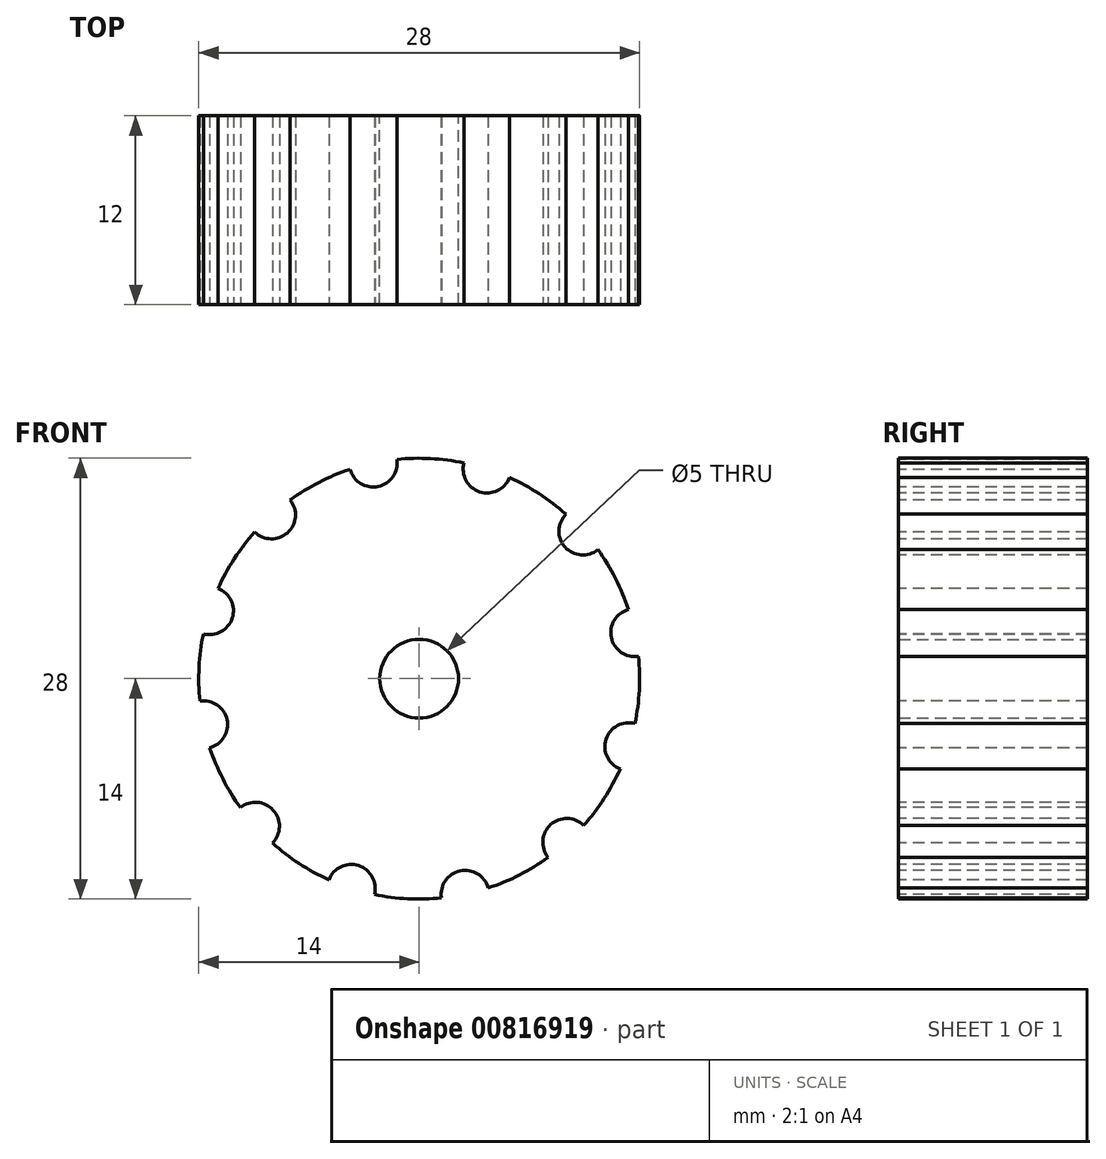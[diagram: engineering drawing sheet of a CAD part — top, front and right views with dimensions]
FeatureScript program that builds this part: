
annotation { "Feature Type Name" : "Feature", "Feature Type Description" : "" }
export const myFeature = defineFeature(function(context is Context, id is Id, definition is map)
    precondition{}
    {
        {
            var Q0;
            Q0=qCreatedBy(makeId("Front.planeOp"),FACE);
            var sketch = newSketch(context, id + "F0", { "sketchPlane" : qUnion([Q0])});
            skPoint(sketch, "E0", {"position": v(0, 0) * mm});
            skCircle(sketch, "E1", {"center": v(0, 0) * mm, "radius": 14 * mm});
            skCircle(sketch, "E2", {"center": v(-7.82, 11.61) * mm, "radius": 1.64 * mm});
            skSolve(sketch);
        }
        {
            var Q0;
            {var subQ0=sQuery(id+"F0.wireOp",EDGE,"E2");var subQ1=sQuery(id+"F0.wireOp",EDGE,"E1");var subQ2=makeQuery(id+"F0.imprint","INTERSECT",VERTEX,{"disambiguationData":[OD(0.0)],"derivedFrom":[subQ1,subQ0]});Q0=makeQuery(id+"F0.imprint","IMPRINT",FACE,{"disambiguationData":[TD([[makeQuery(id+"F0.imprint","IMPRINT",EDGE,{"disambiguationData":[TD([[subQ2,-1.0]])],"derivedFrom":subQ1}),1.0]])]});}
            var Q1;
            {var subQ0=sQuery(id+"F0.wireOp",EDGE,"E2");var subQ1=sQuery(id+"F0.wireOp",EDGE,"E1");var subQ2=makeQuery(id+"F0.imprint","INTERSECT",VERTEX,{"disambiguationData":[OD(0.0)],"derivedFrom":[subQ1,subQ0]});Q1=makeQuery(id+"F0.imprint","IMPRINT",FACE,{"disambiguationData":[TD([[makeQuery(id+"F0.imprint","IMPRINT",EDGE,{"disambiguationData":[TD([[subQ2,1.0]])],"derivedFrom":subQ1}),1.0]])]});}
            extrude(context, id + "F1", {"entities" : qUnion([Q0, Q1]), "depth" : 12 * mm, "offsetDistance" : 25 * mm});
        }
        {
            var Q0;
            Q0=makeQuery(id+"F1.opExtrude","CAP_FACE",FACE,{"disambiguationData":[OSD([sQuery(id+"F0.wireOp",EDGE,"E1")])],"isStart":false});
            var sketch = newSketch(context, id + "F2", { "sketchPlane" : qUnion([Q0])});
            skCircle(sketch, "E3", {"center": v(-9.38, 10.4) * mm, "radius": 1.52 * mm});
            skCircle(sketch, "E4.1.0", {"center": v(-13.32, 4.32) * mm, "radius": 1.52 * mm});
            skCircle(sketch, "E4.2.0", {"center": v(-13.7, -2.92) * mm, "radius": 1.52 * mm});
            skCircle(sketch, "E4.3.0", {"center": v(-10.4, -9.38) * mm, "radius": 1.52 * mm});
            skCircle(sketch, "E4.4.0", {"center": v(-4.32, -13.32) * mm, "radius": 1.52 * mm});
            skCircle(sketch, "E4.5.0", {"center": v(2.92, -13.7) * mm, "radius": 1.52 * mm});
            skCircle(sketch, "E4.6.0", {"center": v(9.38, -10.4) * mm, "radius": 1.52 * mm});
            skCircle(sketch, "E4.7.0", {"center": v(13.32, -4.32) * mm, "radius": 1.52 * mm});
            skCircle(sketch, "E4.8.0", {"center": v(13.7, 2.92) * mm, "radius": 1.52 * mm});
            skCircle(sketch, "E4.9.0", {"center": v(10.4, 9.38) * mm, "radius": 1.52 * mm});
            skCircle(sketch, "E4.10.0", {"center": v(4.32, 13.32) * mm, "radius": 1.52 * mm});
            skCircle(sketch, "E4.11.0", {"center": v(-2.92, 13.7) * mm, "radius": 1.52 * mm});
            skPoint(sketch, "E4.center", {"position": v(0, 0) * mm});
            skSolve(sketch);
        }
        {
            var Q0;
            {var subQ0=sQuery(id+"F2.wireOp",EDGE,"E4.10.0");var subQ1=makeQuery(id+"F1.opExtrude","CAP_EDGE",EDGE,{"disambiguationData":[OSD([sQuery(id+"F0.wireOp",EDGE,"E1")])],"isStart":false});var subQ2=makeQuery(id+"F2.imprint","INTERSECT",VERTEX,{"disambiguationData":[OD(0.0)],"derivedFrom":[subQ1,subQ0]});Q0=makeQuery(id+"F2.imprint","IMPRINT",FACE,{"disambiguationData":[TD([[makeQuery(id+"F2.imprint","IMPRINT",EDGE,{"disambiguationData":[TD([[subQ2,1.0]])],"derivedFrom":subQ0}),1.0]])]});}
            var Q1;
            {var subQ0=sQuery(id+"F2.wireOp",EDGE,"E4.10.0");var subQ1=makeQuery(id+"F1.opExtrude","CAP_EDGE",EDGE,{"disambiguationData":[OSD([sQuery(id+"F0.wireOp",EDGE,"E1")])],"isStart":false});var subQ2=makeQuery(id+"F2.imprint","INTERSECT",VERTEX,{"disambiguationData":[OD(0.0)],"derivedFrom":[subQ1,subQ0]});Q1=makeQuery(id+"F2.imprint","IMPRINT",FACE,{"disambiguationData":[TD([[makeQuery(id+"F2.imprint","IMPRINT",EDGE,{"disambiguationData":[TD([[subQ2,-1.0]])],"derivedFrom":subQ0}),1.0]])]});}
            var Q2;
            {var subQ0=sQuery(id+"F2.wireOp",EDGE,"E4.9.0");var subQ1=makeQuery(id+"F1.opExtrude","CAP_EDGE",EDGE,{"disambiguationData":[OSD([sQuery(id+"F0.wireOp",EDGE,"E1")])],"isStart":false});var subQ2=makeQuery(id+"F2.imprint","INTERSECT",VERTEX,{"disambiguationData":[OD(0.0)],"derivedFrom":[subQ1,subQ0]});Q2=makeQuery(id+"F2.imprint","IMPRINT",FACE,{"disambiguationData":[TD([[makeQuery(id+"F2.imprint","IMPRINT",EDGE,{"disambiguationData":[TD([[subQ2,-1.0]])],"derivedFrom":subQ0}),1.0]])]});}
            var Q3;
            {var subQ0=sQuery(id+"F2.wireOp",EDGE,"E4.9.0");var subQ1=makeQuery(id+"F1.opExtrude","CAP_EDGE",EDGE,{"disambiguationData":[OSD([sQuery(id+"F0.wireOp",EDGE,"E1")])],"isStart":false});var subQ2=makeQuery(id+"F2.imprint","INTERSECT",VERTEX,{"disambiguationData":[OD(0.0)],"derivedFrom":[subQ1,subQ0]});Q3=makeQuery(id+"F2.imprint","IMPRINT",FACE,{"disambiguationData":[TD([[makeQuery(id+"F2.imprint","IMPRINT",EDGE,{"disambiguationData":[TD([[subQ2,1.0]])],"derivedFrom":subQ0}),1.0]])]});}
            var Q4;
            {var subQ0=sQuery(id+"F2.wireOp",EDGE,"E4.8.0");var subQ1=makeQuery(id+"F1.opExtrude","CAP_EDGE",EDGE,{"disambiguationData":[OSD([sQuery(id+"F0.wireOp",EDGE,"E1")])],"isStart":false});var subQ2=makeQuery(id+"F2.imprint","INTERSECT",VERTEX,{"disambiguationData":[OD(0.0)],"derivedFrom":[subQ1,subQ0]});Q4=makeQuery(id+"F2.imprint","IMPRINT",FACE,{"disambiguationData":[TD([[makeQuery(id+"F2.imprint","IMPRINT",EDGE,{"disambiguationData":[TD([[subQ2,-1.0]])],"derivedFrom":subQ0}),1.0]])]});}
            var Q5;
            {var subQ0=sQuery(id+"F2.wireOp",EDGE,"E4.8.0");var subQ1=makeQuery(id+"F1.opExtrude","CAP_EDGE",EDGE,{"disambiguationData":[OSD([sQuery(id+"F0.wireOp",EDGE,"E1")])],"isStart":false});var subQ2=makeQuery(id+"F2.imprint","INTERSECT",VERTEX,{"disambiguationData":[OD(0.0)],"derivedFrom":[subQ1,subQ0]});Q5=makeQuery(id+"F2.imprint","IMPRINT",FACE,{"disambiguationData":[TD([[makeQuery(id+"F2.imprint","IMPRINT",EDGE,{"disambiguationData":[TD([[subQ2,1.0]])],"derivedFrom":subQ0}),1.0]])]});}
            var Q6;
            {var subQ0=sQuery(id+"F2.wireOp",EDGE,"E4.7.0");var subQ1=makeQuery(id+"F1.opExtrude","CAP_EDGE",EDGE,{"disambiguationData":[OSD([sQuery(id+"F0.wireOp",EDGE,"E1")])],"isStart":false});var subQ2=makeQuery(id+"F2.imprint","INTERSECT",VERTEX,{"disambiguationData":[OD(0.0)],"derivedFrom":[subQ1,subQ0]});Q6=makeQuery(id+"F2.imprint","IMPRINT",FACE,{"disambiguationData":[TD([[makeQuery(id+"F2.imprint","IMPRINT",EDGE,{"disambiguationData":[TD([[subQ2,1.0]])],"derivedFrom":subQ0}),1.0]])]});}
            var Q7;
            {var subQ0=sQuery(id+"F2.wireOp",EDGE,"E4.7.0");var subQ1=makeQuery(id+"F1.opExtrude","CAP_EDGE",EDGE,{"disambiguationData":[OSD([sQuery(id+"F0.wireOp",EDGE,"E1")])],"isStart":false});var subQ2=makeQuery(id+"F2.imprint","INTERSECT",VERTEX,{"disambiguationData":[OD(0.0)],"derivedFrom":[subQ1,subQ0]});Q7=makeQuery(id+"F2.imprint","IMPRINT",FACE,{"disambiguationData":[TD([[makeQuery(id+"F2.imprint","IMPRINT",EDGE,{"disambiguationData":[TD([[subQ2,-1.0]])],"derivedFrom":subQ0}),1.0]])]});}
            var Q8;
            {var subQ0=sQuery(id+"F2.wireOp",EDGE,"E4.6.0");var subQ1=makeQuery(id+"F1.opExtrude","CAP_EDGE",EDGE,{"disambiguationData":[OSD([sQuery(id+"F0.wireOp",EDGE,"E1")])],"isStart":false});var subQ2=makeQuery(id+"F2.imprint","INTERSECT",VERTEX,{"disambiguationData":[OD(0.0)],"derivedFrom":[subQ1,subQ0]});Q8=makeQuery(id+"F2.imprint","IMPRINT",FACE,{"disambiguationData":[TD([[makeQuery(id+"F2.imprint","IMPRINT",EDGE,{"disambiguationData":[TD([[subQ2,1.0]])],"derivedFrom":subQ0}),1.0]])]});}
            var Q9;
            {var subQ0=sQuery(id+"F2.wireOp",EDGE,"E4.5.0");var subQ1=makeQuery(id+"F1.opExtrude","CAP_EDGE",EDGE,{"disambiguationData":[OSD([sQuery(id+"F0.wireOp",EDGE,"E1")])],"isStart":false});var subQ2=makeQuery(id+"F2.imprint","INTERSECT",VERTEX,{"disambiguationData":[OD(0.0)],"derivedFrom":[subQ1,subQ0]});Q9=makeQuery(id+"F2.imprint","IMPRINT",FACE,{"disambiguationData":[TD([[makeQuery(id+"F2.imprint","IMPRINT",EDGE,{"disambiguationData":[TD([[subQ2,-1.0]])],"derivedFrom":subQ0}),1.0]])]});}
            var Q10;
            {var subQ0=sQuery(id+"F2.wireOp",EDGE,"E4.5.0");var subQ1=makeQuery(id+"F1.opExtrude","CAP_EDGE",EDGE,{"disambiguationData":[OSD([sQuery(id+"F0.wireOp",EDGE,"E1")])],"isStart":false});var subQ2=makeQuery(id+"F2.imprint","INTERSECT",VERTEX,{"disambiguationData":[OD(0.0)],"derivedFrom":[subQ1,subQ0]});Q10=makeQuery(id+"F2.imprint","IMPRINT",FACE,{"disambiguationData":[TD([[makeQuery(id+"F2.imprint","IMPRINT",EDGE,{"disambiguationData":[TD([[subQ2,1.0]])],"derivedFrom":subQ0}),1.0]])]});}
            var Q11;
            {var subQ0=sQuery(id+"F2.wireOp",EDGE,"E4.4.0");var subQ1=makeQuery(id+"F1.opExtrude","CAP_EDGE",EDGE,{"disambiguationData":[OSD([sQuery(id+"F0.wireOp",EDGE,"E1")])],"isStart":false});var subQ2=makeQuery(id+"F2.imprint","INTERSECT",VERTEX,{"disambiguationData":[OD(0.0)],"derivedFrom":[subQ1,subQ0]});Q11=makeQuery(id+"F2.imprint","IMPRINT",FACE,{"disambiguationData":[TD([[makeQuery(id+"F2.imprint","IMPRINT",EDGE,{"disambiguationData":[TD([[subQ2,1.0]])],"derivedFrom":subQ0}),1.0]])]});}
            var Q12;
            {var subQ0=sQuery(id+"F2.wireOp",EDGE,"E4.3.0");var subQ1=makeQuery(id+"F1.opExtrude","CAP_EDGE",EDGE,{"disambiguationData":[OSD([sQuery(id+"F0.wireOp",EDGE,"E1")])],"isStart":false});var subQ2=makeQuery(id+"F2.imprint","INTERSECT",VERTEX,{"disambiguationData":[OD(0.0)],"derivedFrom":[subQ1,subQ0]});Q12=makeQuery(id+"F2.imprint","IMPRINT",FACE,{"disambiguationData":[TD([[makeQuery(id+"F2.imprint","IMPRINT",EDGE,{"disambiguationData":[TD([[subQ2,1.0]])],"derivedFrom":subQ0}),1.0]])]});}
            var Q13;
            {var subQ0=sQuery(id+"F2.wireOp",EDGE,"E4.2.0");var subQ1=makeQuery(id+"F1.opExtrude","CAP_EDGE",EDGE,{"disambiguationData":[OSD([sQuery(id+"F0.wireOp",EDGE,"E1")])],"isStart":false});var subQ2=makeQuery(id+"F2.imprint","INTERSECT",VERTEX,{"disambiguationData":[OD(0.0)],"derivedFrom":[subQ1,subQ0]});Q13=makeQuery(id+"F2.imprint","IMPRINT",FACE,{"disambiguationData":[TD([[makeQuery(id+"F2.imprint","IMPRINT",EDGE,{"disambiguationData":[TD([[subQ2,-1.0]])],"derivedFrom":subQ0}),1.0]])]});}
            var Q14;
            {var subQ0=sQuery(id+"F2.wireOp",EDGE,"E4.1.0");var subQ1=makeQuery(id+"F1.opExtrude","CAP_EDGE",EDGE,{"disambiguationData":[OSD([sQuery(id+"F0.wireOp",EDGE,"E1")])],"isStart":false});var subQ2=makeQuery(id+"F2.imprint","INTERSECT",VERTEX,{"disambiguationData":[OD(0.0)],"derivedFrom":[subQ1,subQ0]});Q14=makeQuery(id+"F2.imprint","IMPRINT",FACE,{"disambiguationData":[TD([[makeQuery(id+"F2.imprint","IMPRINT",EDGE,{"disambiguationData":[TD([[subQ2,-1.0]])],"derivedFrom":subQ0}),1.0]])]});}
            var Q15;
            {var subQ0=sQuery(id+"F2.wireOp",EDGE,"E3");var subQ1=makeQuery(id+"F1.opExtrude","CAP_EDGE",EDGE,{"disambiguationData":[OSD([sQuery(id+"F0.wireOp",EDGE,"E1")])],"isStart":false});var subQ2=makeQuery(id+"F2.imprint","INTERSECT",VERTEX,{"disambiguationData":[OD(0.0)],"derivedFrom":[subQ1,subQ0]});Q15=makeQuery(id+"F2.imprint","IMPRINT",FACE,{"disambiguationData":[TD([[makeQuery(id+"F2.imprint","IMPRINT",EDGE,{"disambiguationData":[TD([[subQ2,-1.0]])],"derivedFrom":subQ0}),1.0]])]});}
            var Q16;
            {var subQ0=sQuery(id+"F2.wireOp",EDGE,"E4.11.0");var subQ1=makeQuery(id+"F1.opExtrude","CAP_EDGE",EDGE,{"disambiguationData":[OSD([sQuery(id+"F0.wireOp",EDGE,"E1")])],"isStart":false});var subQ2=makeQuery(id+"F2.imprint","INTERSECT",VERTEX,{"disambiguationData":[OD(0.0)],"derivedFrom":[subQ1,subQ0]});Q16=makeQuery(id+"F2.imprint","IMPRINT",FACE,{"disambiguationData":[TD([[makeQuery(id+"F2.imprint","IMPRINT",EDGE,{"disambiguationData":[TD([[subQ2,-1.0]])],"derivedFrom":subQ0}),1.0]])]});}
            extrude(context, id + "F3", {"entities" : qUnion([Q0, Q1, Q2, Q3, Q4, Q5, Q6, Q7, Q8, Q9, Q10, Q11, Q12, Q13, Q14, Q15, Q16]), "operationType" : NewBodyOperationType.REMOVE, "oppositeDirection" : true, "depth" : 25 * mm, "offsetDistance" : 25 * mm});
        }
        {
            var Q0;
            Q0=makeQuery(id+"F1.opExtrude","CAP_FACE",FACE,{"disambiguationData":[OSD([sQuery(id+"F0.wireOp",EDGE,"E1")])],"isStart":true});
            var sketch = newSketch(context, id + "F4", { "sketchPlane" : qUnion([Q0])});
            skPoint(sketch, "E5", {"position": v(0, 0) * mm});
            skSolve(sketch);
        }
        {
            var Q0;
            Q0=sQuery(id+"F4.wireOp",VERTEX,"E5");
            var Q1;
            Q1=makeQuery(id+"F1.opExtrude","SWEPT_BODY",BODY,{"disambiguationData":[OSD([sQuery(id+"F0.wireOp",EDGE,"E1")])]});
            hole(context, id + "F5", {"style" : HoleStyle.SIMPLE, "endStyle" : HoleEndStyle.THROUGH, "holeDiameter" : 5 * mm, "majorDiameter" : 5 * mm, "isTappedThrough" : true, "tappedDepth" : 12 * mm, "tapClearance" : 3, "startFromSketch" : true, "locations" : qUnion([Q0]), "scope" : qUnion([Q1])});
        }
    });
